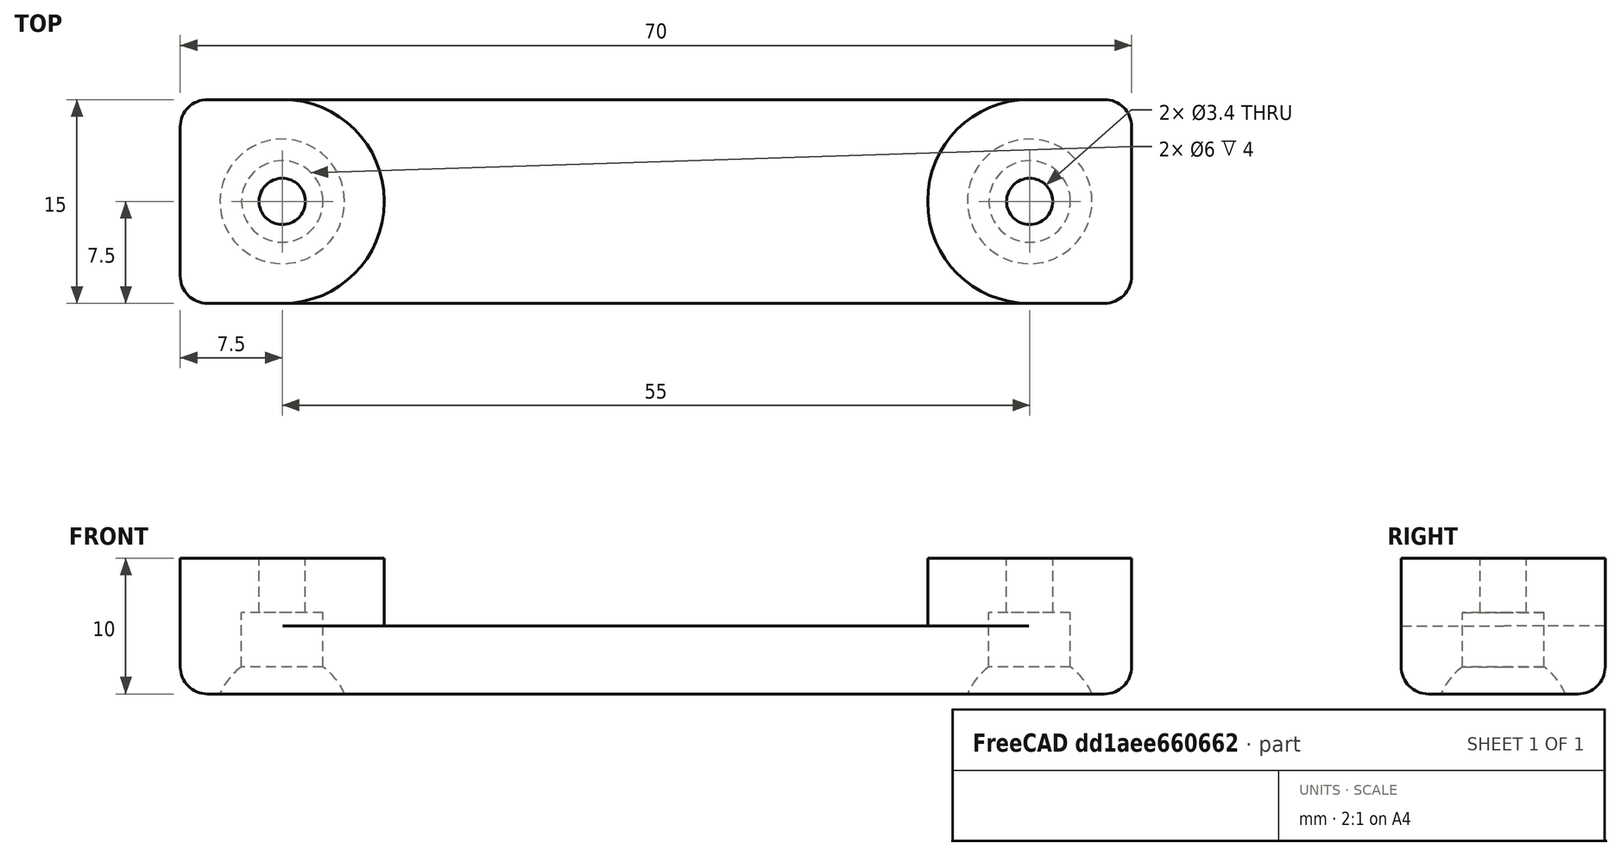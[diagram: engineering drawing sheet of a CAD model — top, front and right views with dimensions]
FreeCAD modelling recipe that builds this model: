
FCSTD DOCUMENT  (FreeCAD 0.14R3703 (Git))
Label: GOUM_Roller_Alu_Mount2
License: CC-BY 3.0
LicenseURL: http://creativecommons.org/licenses/by/3.0/
objects: Part::Cut×7, Part::Cylinder×4, Part::Fillet×3, Part::Box×2, Part::Sphere×2
note: 18 computed .brp shape members not serialized (recipe doc carries the construction recipe); baked Part::Feature solids carry a one-line shape summary decoded from their .brp

FEATURE [Part::Box] Box  label="Cube"
  Height = 10
  Length = 70
  Width = 15
FEATURE [Part::Cylinder] Cylinder
  Angle = 360
  Height = 10
  Placement = pos=(7.5,7.5,0) rot=(0,0,1;0rad)
  Radius = 1.7
FEATURE [Part::Cylinder] Cylinder001
  Angle = 360
  Height = 10
  Placement = pos=(62.5,7.5,0) rot=(0,0,1;0rad)
  Radius = 1.7
FEATURE [Part::Fillet] Fillet
  Base = -> Box
  Edges = 4 edges r=2: [Edge1,Edge3,Edge5,Edge7]
FEATURE [Part::Fillet] Fillet001
  Base = -> Fillet
  Edges = 8 edges r=2: [Edge4,Edge12,Edge14,Edge16,Edge17,Edge18,Edge19,Edge20]
FEATURE [Part::Cut] Cut
  Base = -> Fillet001
  Tool = -> Cylinder
FEATURE [Part::Cut] Cut001
  Base = -> Cut
  Tool = -> Cylinder001
FEATURE [Part::Cylinder] Cylinder002
  Angle = 360
  Height = 6
  Placement = pos=(7.5,7.5,0) rot=(0,0,1;0rad)
  Radius = 3
FEATURE [Part::Cylinder] Cylinder003
  Angle = 360
  Height = 6
  Placement = pos=(62.5,7.5,0) rot=(0,0,1;0rad)
  Radius = 3
FEATURE [Part::Cut] Cut002
  Base = -> Cut001
  Tool = -> Cylinder002
FEATURE [Part::Cut] Cut003
  Base = -> Cut002
  Tool = -> Cylinder003
FEATURE [Part::Sphere] Sphere
  Angle1 = -90
  Angle2 = 90
  Angle3 = 360
  Placement = pos=(7.5,7.5,-2) rot=(0,0,1;0rad)
  Radius = 5
FEATURE [Part::Sphere] Sphere001
  Angle1 = -90
  Angle2 = 90
  Angle3 = 360
  Placement = pos=(62.5,7.5,-2) rot=(0,0,1;0rad)
  Radius = 5
FEATURE [Part::Cut] Cut004
  Base = -> Cut003
  Tool = -> Sphere
FEATURE [Part::Cut] Cut005
  Base = -> Cut004
  Tool = -> Sphere001
FEATURE [Part::Box] Box001  label="Cube001"
  Height = 5
  Length = 40
  Placement = pos=(15,0,5) rot=(0,0,1;0rad)
  Width = 15
FEATURE [Part::Cut] Cut006
  Base = -> Cut005
  Tool = -> Box001
FEATURE [Part::Fillet] Fillet002  label="PRINT2_Misumi-top-mount"
  Base = -> Cut006
  Edges = 4 edges r=7.45: [Edge23,Edge25,Edge36,Edge38]
